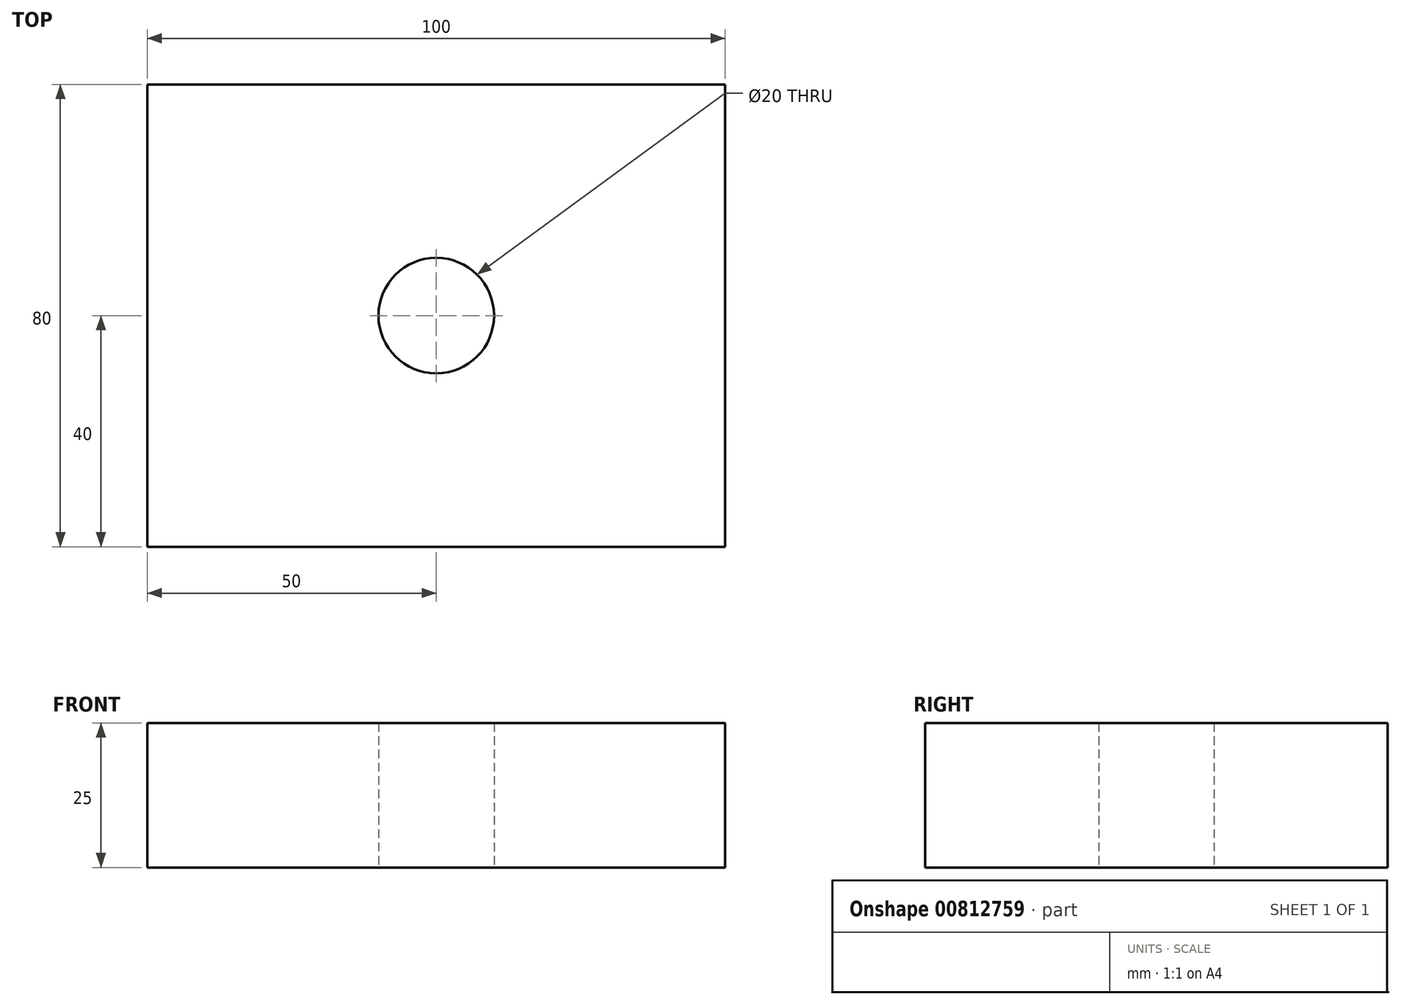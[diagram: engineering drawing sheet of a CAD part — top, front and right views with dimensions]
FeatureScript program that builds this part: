
annotation { "Feature Type Name" : "Feature", "Feature Type Description" : "" }
export const myFeature = defineFeature(function(context is Context, id is Id, definition is map)
    precondition{}
    {
        {
            var Q0;
            Q0=qCreatedBy(makeId("Top.planeOp"),FACE);
            var sketch = newSketch(context, id + "F0", { "sketchPlane" : qUnion([Q0])});
            skLineSegment(sketch, "E0.bottom", {"start": v(-50, 40) * mm, "end": v(50, 40) * mm});
            skLineSegment(sketch, "E0.top", {"start": v(-50, -40) * mm, "end": v(50, -40) * mm});
            skLineSegment(sketch, "E0.left", {"start": v(-50, 40) * mm, "end": v(-50, -40) * mm});
            skLineSegment(sketch, "E0.right", {"start": v(50, 40) * mm, "end": v(50, -40) * mm});
            skCircle(sketch, "E1", {"center": v(0, 0) * mm, "radius": 10 * mm});
            skSolve(sketch);
        }
        {
            var Q0;
            Q0=makeQuery(id+"F0.imprint","IMPRINT",FACE,{"disambiguationData":[TD([[makeQuery(id+"F0.imprint","IMPRINT",EDGE,{"derivedFrom":sQuery(id+"F0.wireOp",EDGE,"E0.bottom")}),-1.0]])]});
            extrude(context, id + "F1", {"entities" : qUnion([Q0]), "depth" : 25 * mm, "offsetDistance" : 25 * mm});
        }
    });
